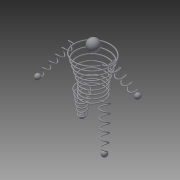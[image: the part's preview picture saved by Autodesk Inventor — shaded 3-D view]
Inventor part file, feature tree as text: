
AUTODESK INVENTOR PART (.ipt)
format: ipt  version: 2015 SP2 (Build 190223200, 223)  size: 838,656 bytes
history: native  units: mm
features: other x21, plane x4
ambient origin geometry x8: Origin, YZ Plane, XZ Plane, XY Plane, X Axis, Y Axis, Z Axis, Center Point
bodies: Volumenkörper7 (feature_tree), Volumenkörper8 (feature_tree), Volumenkörper9 (feature_tree), Volumenkörper10 (feature_tree), Volumenkörper11 (feature_tree), Volumenkörper12 (feature_tree), Volumenkörper13 (feature_tree)
feature tree (25):
  other  "3D-Skizze1"
  other  "Arbeitsachse3"
  plane  "Arbeitsebene7"
  other  "Hand_Arm_R"
  other  "Hand_R"
  other  "Arm_R"
  plane  "Arbeitsebene8"
  other  "Hand_Arm_L"
  other  "Hand_L"
  other  "Arm_L"
  other  "Head_Torso"
  other  "Head"
  other  "Torso_U"
  other  "Torso_B"
  other  "Arbeitsachse5"
  other  "Arbeitsachse6"
  other  "Arbeitsachse7"
  plane  "Arbeitsebene9"
  plane  "Arbeitsebene10"
  other  "Foot_Leg_R"
  other  "Foot_R"
  other  "Leg_R"
  other  "Foot_Leg_L"
  other  "Foot_L"
  other  "Leg_L"
